# Revit family: Faucet-Delta-TRINSIC-Single_Handle_Wall_Mount_Lavatory_Faucet_Trim
name_source: partatom
category: Plumbing Fixtures
revit_build: Autodesk Revit Architecture 2014 (Build: 20140709_2115(x64)
units: mm (PartAtom-declared; Revit-internal decimal feet)

## types (4) — shared parameters
ADA Compliant = Yes
Actual Valve Water Flow = 1 GPM
CWC R = 0"
Cold Water Connection = 1"
Default Elevation = 3' - 9 1/4"
Depth = 0' - 4 15/16"
Description = Trinsic - Two Hole On Wall
Flow Rate = 1.20 gpm @ 60 psi | 4.5 L/min @ 414 kPa

Read more: http://www.deltafaucet.com
HWC R = 0"
Height = 0' - 6 5/8"
Hot Water Connection = 1"
Manufacturer = DELTA
Product Documentation Link = http://www.deltafaucet.com
Product Name = Single Handle Wall Mount Lavatory Faucet Trim
Product Page URL = http://www.deltafaucet.com
Series = Trinsic
URL = http://www.deltafaucet.com
Warranty = http://www.deltafaucet.com
Width = 0' - 4"

## per-type parameters (varying)
| type | Finish |
| T3559LF-WL | Chrome - DELTA - Polished |
| T3559LF-CZWL | Champagne - DELTA - Bronze |
| T3559LF-RBWL | Venetian - DELTA - Bronze |
| T3559LF-SSWL | Steel - DELTA - Brilliance Stainless |

note: column(s) folded — value = type name in every type: Model

## geometry (parser evidence)
native form markers: Blend x12, Sweep x1
no freeform markers — native parametric forms only
